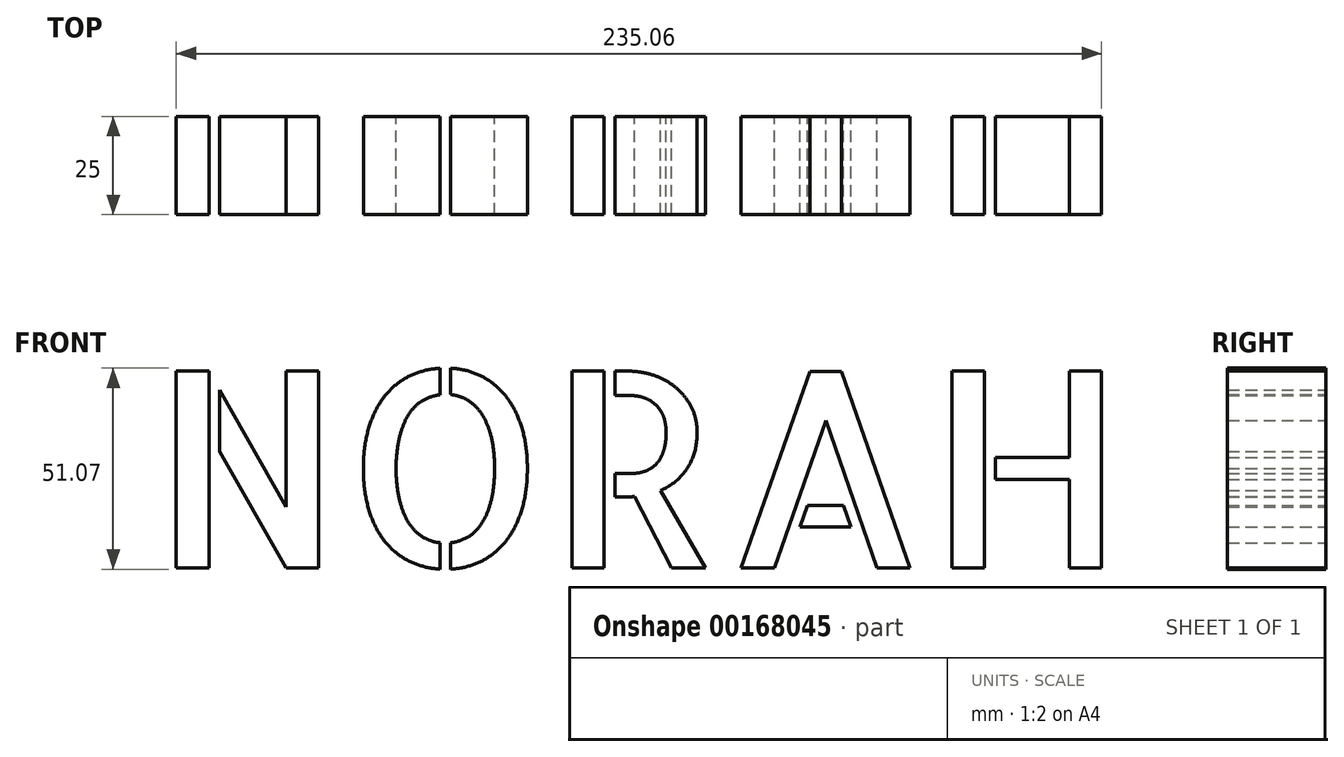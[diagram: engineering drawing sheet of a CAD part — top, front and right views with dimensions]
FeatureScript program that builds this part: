
annotation { "Feature Type Name" : "Feature", "Feature Type Description" : "" }
export const myFeature = defineFeature(function(context is Context, id is Id, definition is map)
    precondition{}
    {
        {
            var Q0;
            Q0=qCreatedBy(makeId("Front.planeOp"),FACE);
            var sketch = newSketch(context, id + "F0", { "sketchPlane" : qUnion([Q0])});
            skText(sketch, "E0", { "text": "NORAH", "fontName": "AllertaStencil-Regular.ttf"});
            const initialGuessF0  = {"E0": [-0.12297, 0, 1, 0, 0.05]};
            skSetInitialGuess(sketch, initialGuessF0);
            skSolve(sketch);
        }
        {
            var Q0;
            Q0 = qSketchRegion(id + "F0", true);
            extrude(context, id + "F1", {"entities" : qUnion([Q0]), "depth" : 25 * mm});
        }
    });
